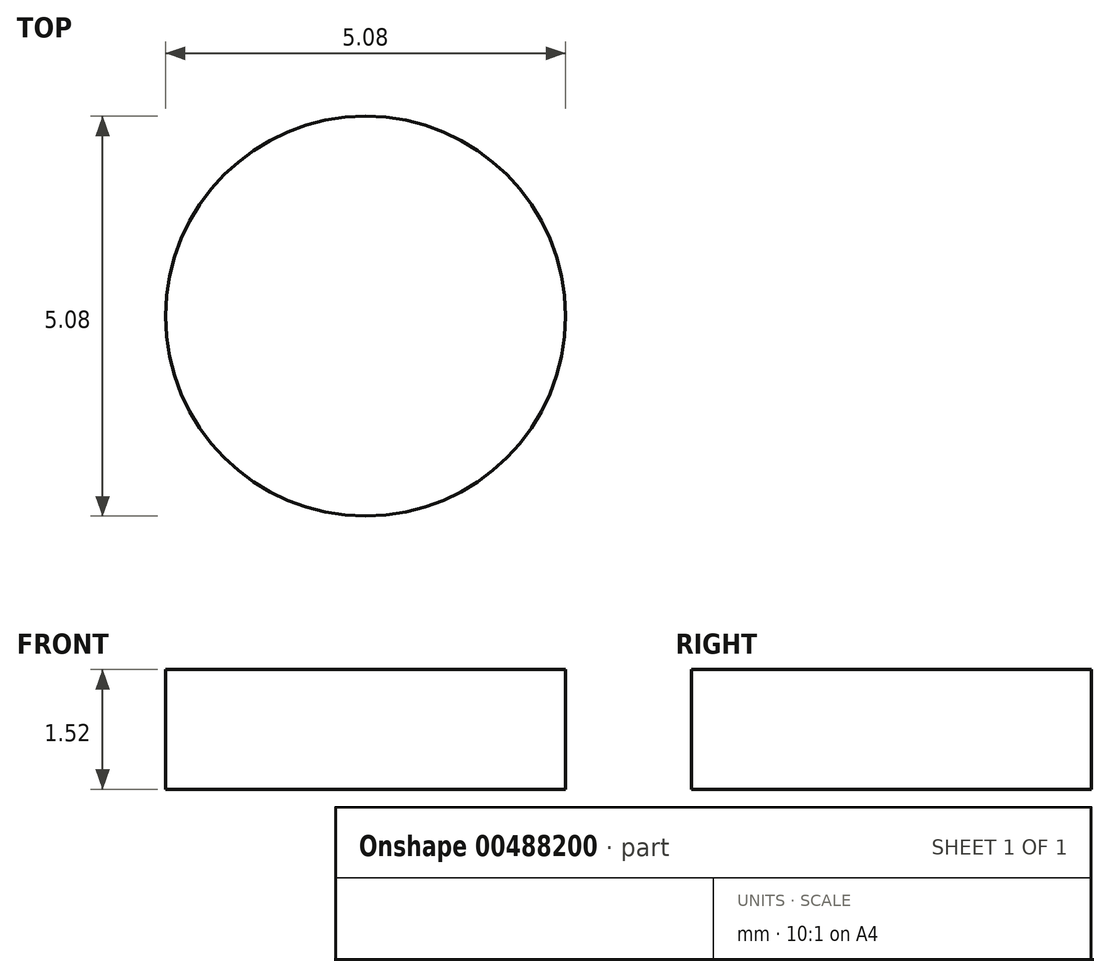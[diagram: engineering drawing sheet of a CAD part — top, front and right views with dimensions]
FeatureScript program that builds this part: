
annotation { "Feature Type Name" : "Feature", "Feature Type Description" : "" }
export const myFeature = defineFeature(function(context is Context, id is Id, definition is map)
    precondition{}
    {
        {
            var Q0;
            Q0=qCreatedBy(makeId("Top.planeOp"),FACE);
            var sketch = newSketch(context, id + "F0", { "sketchPlane" : qUnion([Q0])});
            skCircle(sketch, "E0", {"center": v(0, 0) * mm, "radius": 2.54 * mm});
            skSolve(sketch);
        }
        {
            var Q0;
            Q0 = qSketchRegion(id + "F0", true);
            extrude(context, id + "F1", {"entities" : qUnion([Q0]), "depth" : 1.52 * mm, "offsetDistance" : 25.4 * mm});
        }
    });
